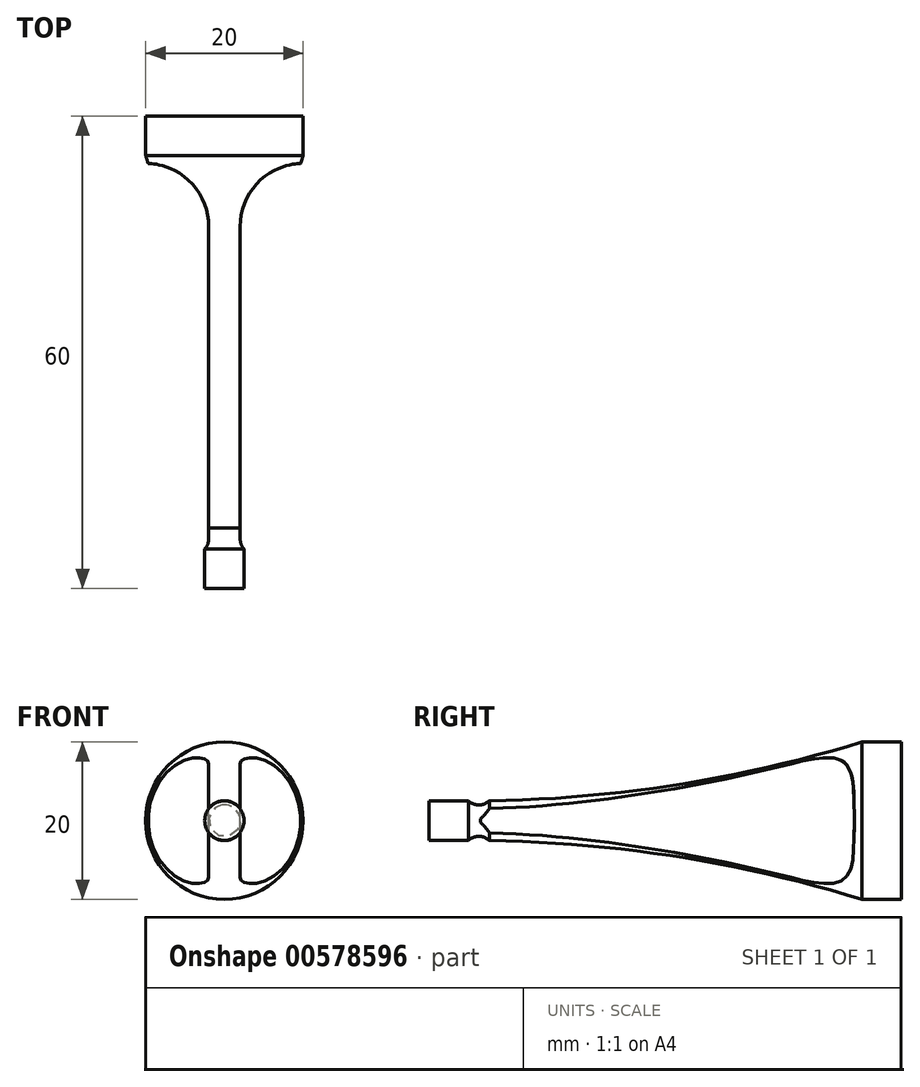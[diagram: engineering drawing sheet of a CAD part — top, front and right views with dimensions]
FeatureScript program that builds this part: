
annotation { "Feature Type Name" : "Feature", "Feature Type Description" : "" }
export const myFeature = defineFeature(function(context is Context, id is Id, definition is map)
    precondition{}
    {
        {
            var Q0;
            Q0=qCreatedBy(makeId("Right.planeOp"),FACE);
            var sketch = newSketch(context, id + "F0", { "sketchPlane" : qUnion([Q0])});
            skLineSegment(sketch, "E0", {"start": v(39.05, 0) * mm, "end": v(-78.02, 0) * mm, "construction": true});
            skLineSegment(sketch, "E1", {"start": v(0, 0) * mm, "end": v(0, 10) * mm});
            skLineSegment(sketch, "E2", {"start": v(0, 10) * mm, "end": v(-5, 10) * mm});
            skLineSegment(sketch, "E3", {"start": v(0, 0) * mm, "end": v(-60, 0) * mm});
            skLineSegment(sketch, "E4", {"start": v(-60, 0) * mm, "end": v(-60, 2.5) * mm});
            skLineSegment(sketch, "E5", {"start": v(-60, 2.5) * mm, "end": v(-55, 2.5) * mm});
            skArc(sketch, "E6", {"start": v(-52.33, 2.52) * mm, "mid": v(-28.4, 4.59) * mm, "end": v(-5, 10) * mm});
            skArc(sketch, "E7", {"start": v(-55, 2.5) * mm, "mid": v(-53.66, 2) * mm, "end": v(-52.33, 2.52) * mm});
            skSolve(sketch);
        }
        {
            var Q0;
            Q0=qSketchRegion(id+"F0",true);
            var Q1;
            Q1=sQuery(id+"F0.wireOp",EDGE,"E0");
            revolve(context, id + "F1", {"entities" : qUnion([Q0]), "axis" : qUnion([Q1]), "revolveType" : RevolveType.FULL});
        }
        {
            var Q0;
            Q0=qCreatedBy(makeId("Top.planeOp"),FACE);
            var sketch = newSketch(context, id + "F2", { "sketchPlane" : qUnion([Q0])});
            skLineSegment(sketch, "E8", {"start": v(2, -53.5) * mm, "end": v(2, -14) * mm});
            skArc(sketch, "E9", {"start": v(10, -6) * mm, "mid": v(4.34, -8.34) * mm, "end": v(2, -14) * mm});
            skLineSegment(sketch, "E10", {"start": v(10, 2.45) * mm, "end": v(10, -6) * mm, "construction": true});
            skLineSegment(sketch, "E11", {"start": v(10, -53.5) * mm, "end": v(2, -53.5) * mm});
            skLineSegment(sketch, "E12", {"start": v(10, -53.5) * mm, "end": v(10, -6) * mm});
            skLineSegment(sketch, "E13", {"start": v(-2, -53.5) * mm, "end": v(-2, -14) * mm});
            skLineSegment(sketch, "E14", {"start": v(0, -71.6) * mm, "end": v(0, 17.57) * mm, "construction": true});
            skArc(sketch, "E15", {"start": v(-2, -14) * mm, "mid": v(-4.34, -8.34) * mm, "end": v(-10, -6) * mm});
            skLineSegment(sketch, "E16", {"start": v(-2, -53.5) * mm, "end": v(-10, -53.5) * mm});
            skLineSegment(sketch, "E17", {"start": v(-10, -53.5) * mm, "end": v(-10, -6) * mm});
            skSolve(sketch);
        }
        {
            var Q0;
            Q0=qSketchRegion(id+"F2",true);
            var Q1;
            Q1=makeQuery(id+"F1.opRevolve","SWEPT_BODY",BODY,{"disambiguationData":[OSD([sQuery(id+"F0.wireOp",EDGE,"E1"),sQuery(id+"F0.wireOp",EDGE,"E2"),sQuery(id+"F0.wireOp",EDGE,"E3"),sQuery(id+"F0.wireOp",EDGE,"E4"),sQuery(id+"F0.wireOp",EDGE,"E5"),sQuery(id+"F0.wireOp",EDGE,"E6"),sQuery(id+"F0.wireOp",EDGE,"E7")])]});
            var Q2;
            Q2=makeQuery(id+"F1.opRevolve","SWEPT_BODY",BODY,{"disambiguationData":[OSD([sQuery(id+"F0.wireOp",EDGE,"E1"),sQuery(id+"F0.wireOp",EDGE,"E2"),sQuery(id+"F0.wireOp",EDGE,"E3"),sQuery(id+"F0.wireOp",EDGE,"E4"),sQuery(id+"F0.wireOp",EDGE,"E5"),sQuery(id+"F0.wireOp",EDGE,"E6"),sQuery(id+"F0.wireOp",EDGE,"E7")])]});
            extrude(context, id + "F3", {"entities" : qUnion([Q0]), "operationType" : NewBodyOperationType.REMOVE, "endBound" : BoundingType.THROUGH_ALL, "oppositeDirection" : true, "depth" : 25 * mm, "endBoundEntityBody" : qUnion([Q1]), "offsetDistance" : 100 * mm, "offsetOppositeDirection" : true, "hasSecondDirection" : true, "secondDirectionBound" : SecondDirectionBoundingType.UP_TO_BODY, "secondDirectionOppositeDirection" : false, "secondDirectionDepth" : 25 * mm, "secondDirectionBoundEntityBody" : qUnion([Q2])});
        }
    });
